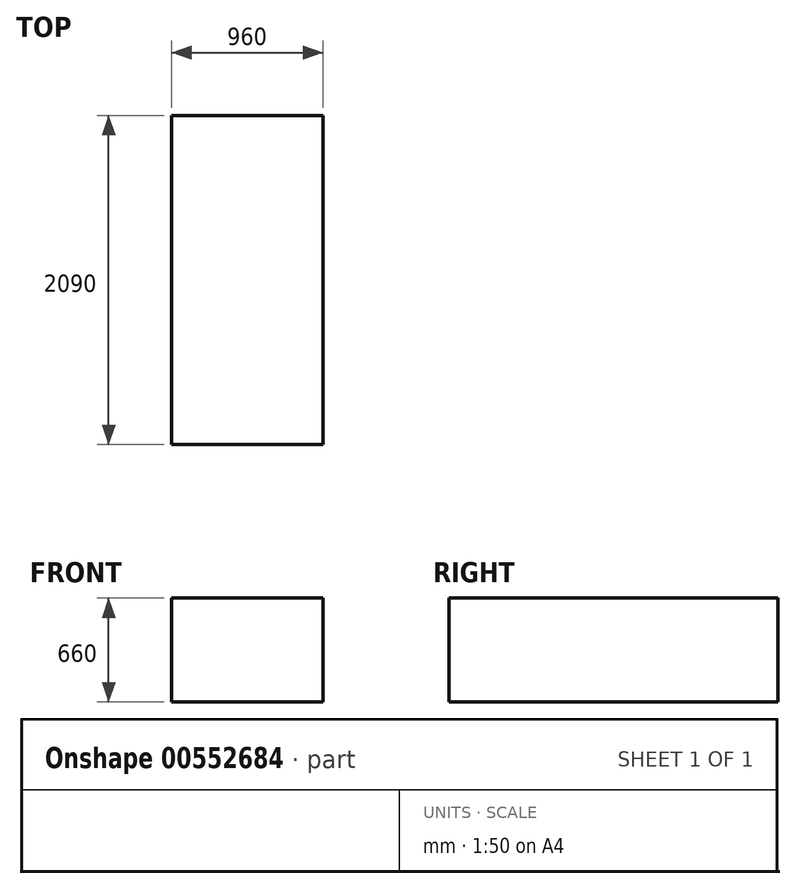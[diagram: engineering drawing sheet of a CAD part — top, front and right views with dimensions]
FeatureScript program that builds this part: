
annotation { "Feature Type Name" : "Feature", "Feature Type Description" : "" }
export const myFeature = defineFeature(function(context is Context, id is Id, definition is map)
    precondition{}
    {
        {
            var Q0;
            Q0=qCreatedBy(makeId("Front.planeOp"),FACE);
            var sketch = newSketch(context, id + "F0", { "sketchPlane" : qUnion([Q0])});
            skLineSegment(sketch, "E0.bottom", {"start": v(480, 330) * mm, "end": v(-480, 330) * mm});
            skLineSegment(sketch, "E0.top", {"start": v(480, -330) * mm, "end": v(-480, -330) * mm});
            skLineSegment(sketch, "E0.left", {"start": v(480, 330) * mm, "end": v(480, -330) * mm});
            skLineSegment(sketch, "E0.right", {"start": v(-480, 330) * mm, "end": v(-480, -330) * mm});
            skPoint(sketch, "E0.middle", {"position": v(0, 0) * mm});
            skSolve(sketch);
        }
        {
            var Q0;
            Q0 = qSketchRegion(id + "F0", true);
            extrude(context, id + "F1", {"entities" : qUnion([Q0]), "oppositeDirection" : true, "depth" : 2090 * mm, "offsetDistance" : 25 * mm});
        }
    });
